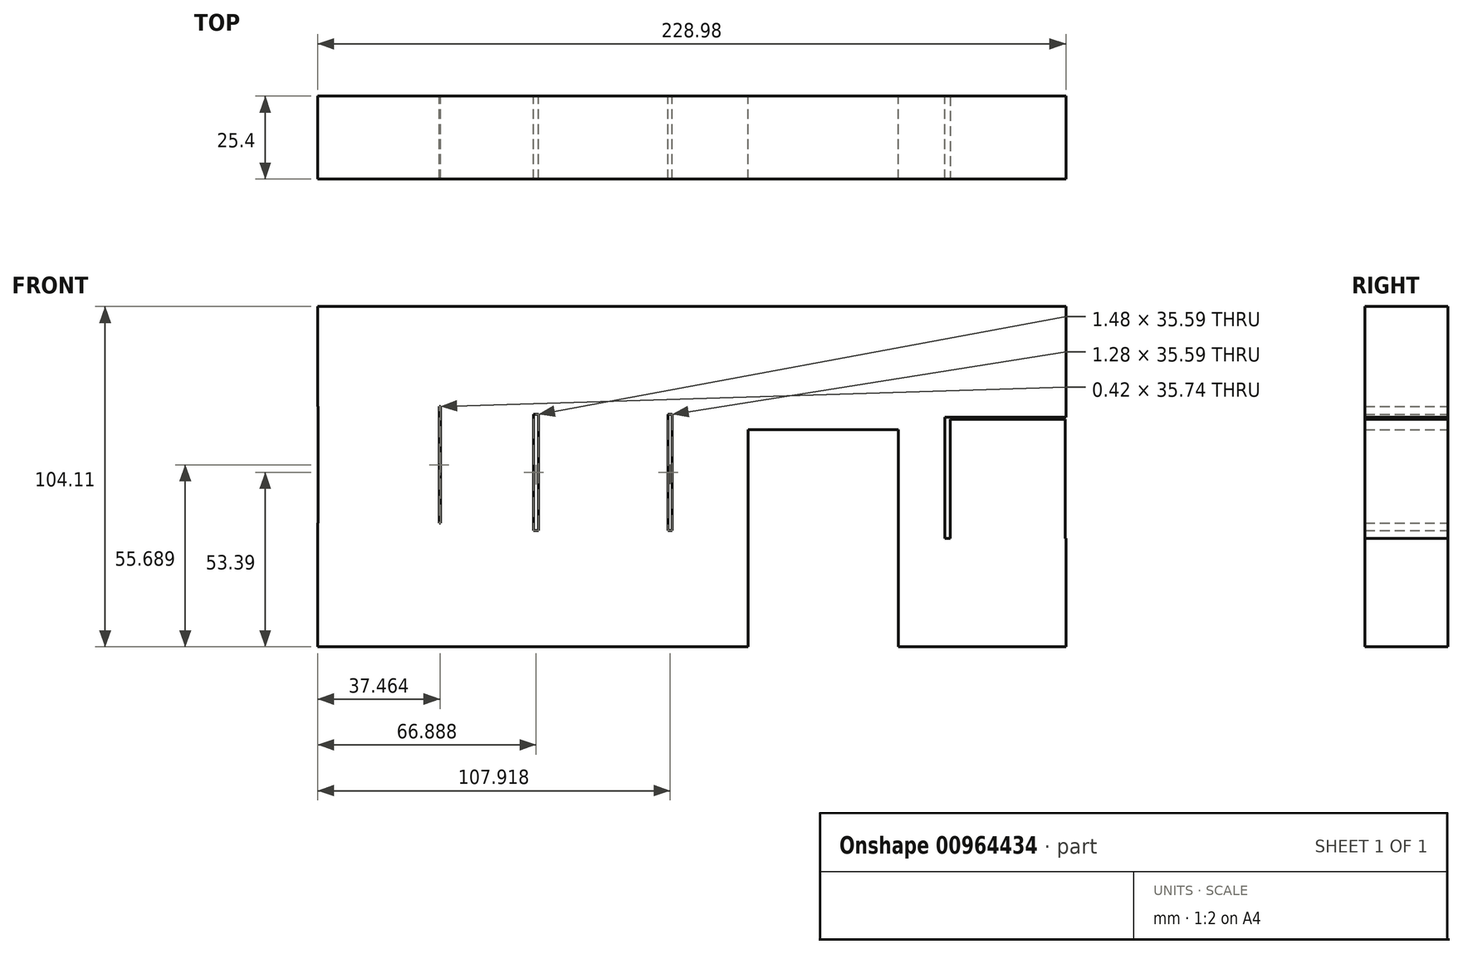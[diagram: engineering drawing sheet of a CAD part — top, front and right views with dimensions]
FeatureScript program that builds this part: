
annotation { "Feature Type Name" : "Feature", "Feature Type Description" : "" }
export const myFeature = defineFeature(function(context is Context, id is Id, definition is map)
    precondition{}
    {
        {
            var Q0;
            Q0=qCreatedBy(makeId("Front.planeOp"),FACE);
            var sketch = newSketch(context, id + "F0", { "sketchPlane" : qUnion([Q0])});
            skLineSegment(sketch, "E0.bottom", {"start": v(-100.93, -37.82) * mm, "end": v(128.05, -37.82) * mm});
            skLineSegment(sketch, "E0.top", {"start": v(-100.93, 66.29) * mm, "end": v(128.05, 66.29) * mm});
            skLineSegment(sketch, "E0.left", {"start": v(-100.93, -37.82) * mm, "end": v(-100.93, 66.29) * mm});
            skLineSegment(sketch, "E0.right", {"start": v(128.05, -37.82) * mm, "end": v(128.05, 66.29) * mm});
            skLineSegment(sketch, "E1.bottom", {"start": v(30.76, -37.82) * mm, "end": v(76.74, -37.82) * mm});
            skLineSegment(sketch, "E1.top", {"start": v(30.76, 28.62) * mm, "end": v(76.74, 28.62) * mm});
            skLineSegment(sketch, "E1.left", {"start": v(30.76, -37.82) * mm, "end": v(30.76, 28.62) * mm});
            skLineSegment(sketch, "E1.right", {"start": v(76.74, -37.82) * mm, "end": v(76.74, 28.62) * mm});
            skLineSegment(sketch, "E2.bottom", {"start": v(90.97, -4.6) * mm, "end": v(128.05, -4.6) * mm});
            skLineSegment(sketch, "E2.top", {"start": v(90.97, 32.48) * mm, "end": v(128.05, 32.48) * mm});
            skLineSegment(sketch, "E2.left", {"start": v(90.97, -4.6) * mm, "end": v(90.97, 32.48) * mm});
            skLineSegment(sketch, "E2.right", {"start": v(128.05, -4.6) * mm, "end": v(128.05, 32.48) * mm});
            skLineSegment(sketch, "E3.bottom", {"start": v(7.63, -2.23) * mm, "end": v(-34.78, -2.23) * mm});
            skLineSegment(sketch, "E3.top", {"start": v(7.63, 33.37) * mm, "end": v(-34.78, 33.37) * mm});
            skLineSegment(sketch, "E3.left", {"start": v(7.63, -2.23) * mm, "end": v(7.63, 33.37) * mm});
            skLineSegment(sketch, "E3.right", {"start": v(-34.78, -2.23) * mm, "end": v(-34.78, 33.37) * mm});
            skLineSegment(sketch, "E4.bottom", {"start": v(-63.26, 0) * mm, "end": v(-100.93, 0) * mm});
            skLineSegment(sketch, "E4.top", {"start": v(-63.26, 35.74) * mm, "end": v(-100.93, 35.74) * mm});
            skLineSegment(sketch, "E4.left", {"start": v(-63.26, 0) * mm, "end": v(-63.26, 35.74) * mm});
            skLineSegment(sketch, "E4.right", {"start": v(-100.93, 0) * mm, "end": v(-100.93, 35.74) * mm});
            skSolve(sketch);
        }
        {
            var Q0;
            {var subQ3=sQuery(id+"F0.wireOp",EDGE,"E0.top");Q0=makeQuery(id+"F0.imprint","IMPRINT",FACE,{"disambiguationData":[TD([[makeQuery(id+"F0.imprint","IMPRINT",EDGE,{"derivedFrom":subQ3}),-1.0]])]});}
            extrude(context, id + "F1", {"entities" : qUnion([Q0]), "depth" : 25.4 * mm, "offsetDistance" : 25.4 * mm});
        }
        {
            var Q0;
            Q0=qCreatedBy(makeId("Front.planeOp"),FACE);
            var sketch = newSketch(context, id + "F2", { "sketchPlane" : qUnion([Q0])});
            skLineSegment(sketch, "E5.bottom", {"start": v(-100.76, 0) * mm, "end": v(-63.68, 0) * mm});
            skLineSegment(sketch, "E5.top", {"start": v(-100.76, 36.23) * mm, "end": v(-63.68, 36.23) * mm});
            skLineSegment(sketch, "E5.left", {"start": v(-100.76, 0) * mm, "end": v(-100.76, 36.23) * mm});
            skLineSegment(sketch, "E5.right", {"start": v(-63.68, 0) * mm, "end": v(-63.68, 36.23) * mm});
            skLineSegment(sketch, "E6.bottom", {"start": v(-33.3, -2.78) * mm, "end": v(6.35, -2.78) * mm});
            skLineSegment(sketch, "E6.top", {"start": v(-33.3, 33.67) * mm, "end": v(6.35, 33.67) * mm});
            skLineSegment(sketch, "E6.left", {"start": v(-33.3, -2.78) * mm, "end": v(-33.3, 33.67) * mm});
            skLineSegment(sketch, "E6.right", {"start": v(6.35, -2.78) * mm, "end": v(6.35, 33.67) * mm});
            skLineSegment(sketch, "E7.bottom", {"start": v(92.67, -5.02) * mm, "end": v(127.84, -5.02) * mm});
            skLineSegment(sketch, "E7.top", {"start": v(92.67, 31.75) * mm, "end": v(127.84, 31.75) * mm});
            skLineSegment(sketch, "E7.left", {"start": v(92.67, -5.02) * mm, "end": v(92.67, 31.75) * mm});
            skLineSegment(sketch, "E7.right", {"start": v(127.84, -5.02) * mm, "end": v(127.84, 31.75) * mm});
            skSolve(sketch);
        }
        {
            var Q0;
            Q0 = qSketchRegion(id + "F2", true);
            extrude(context, id + "F3", {"entities" : qUnion([Q0]), "operationType" : NewBodyOperationType.ADD, "depth" : 25.4 * mm, "offsetDistance" : 25.4 * mm});
        }
    });
